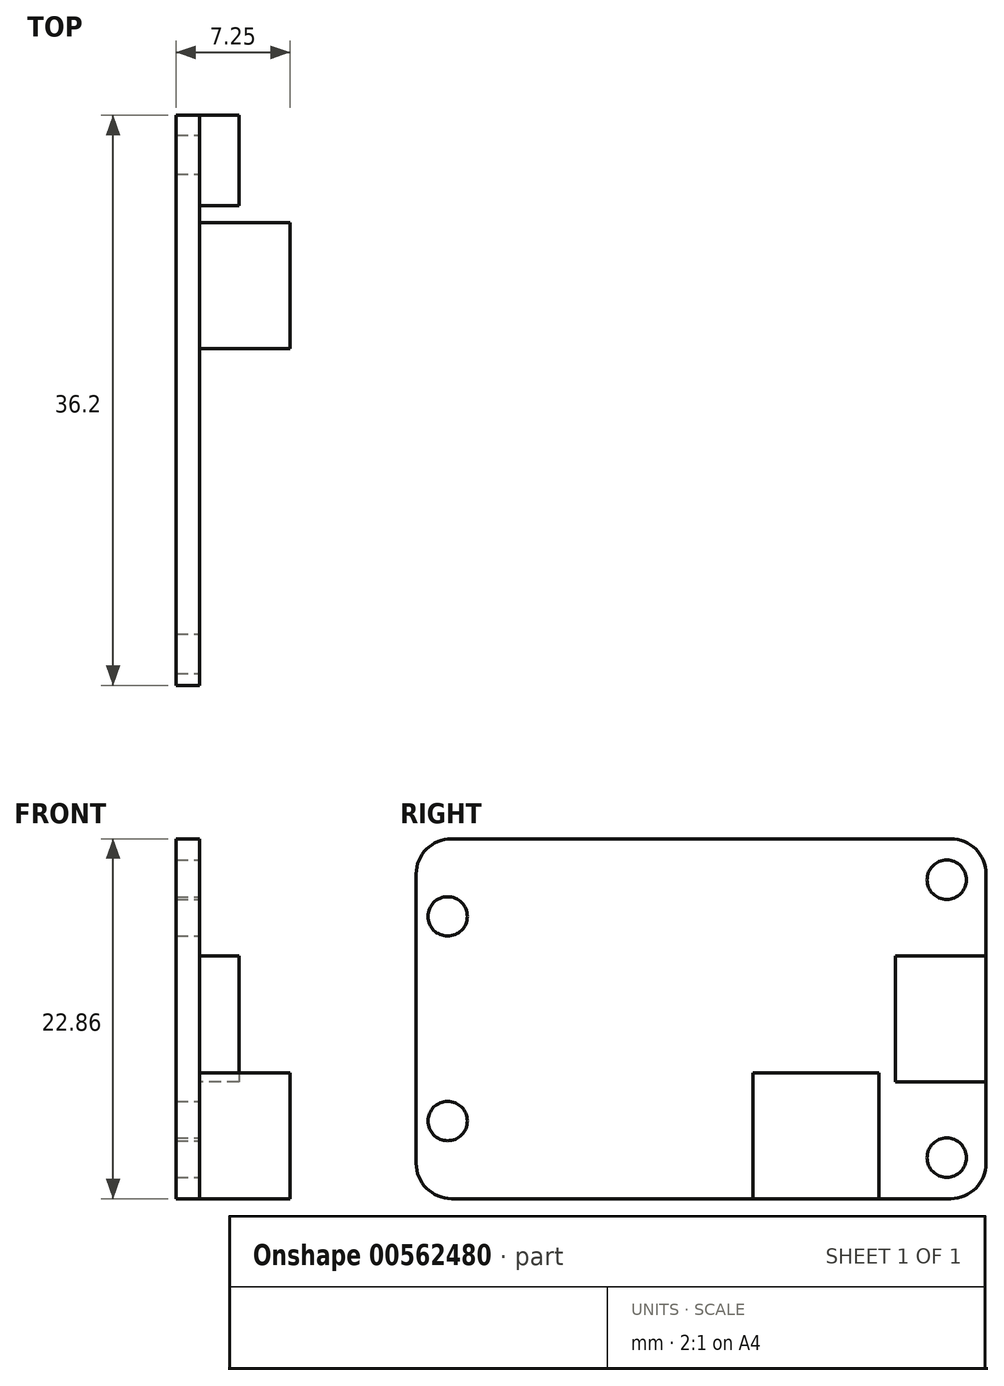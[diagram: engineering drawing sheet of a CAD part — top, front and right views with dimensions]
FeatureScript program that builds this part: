
annotation { "Feature Type Name" : "Feature", "Feature Type Description" : "" }
export const myFeature = defineFeature(function(context is Context, id is Id, definition is map)
    precondition{}
    {
        {
            var Q0;
            Q0=qCreatedBy(makeId("Right.planeOp"),FACE);
            var sketch = newSketch(context, id + "F0", { "sketchPlane" : qUnion([Q0])});
            skLineSegment(sketch, "E0.bottom", {"start": v(-18.1, 11.43) * mm, "end": v(18.1, 11.43) * mm});
            skLineSegment(sketch, "E0.top", {"start": v(-18.1, -11.43) * mm, "end": v(18.1, -11.43) * mm});
            skLineSegment(sketch, "E0.left", {"start": v(-18.1, 11.43) * mm, "end": v(-18.1, -11.43) * mm});
            skLineSegment(sketch, "E0.right", {"start": v(18.1, 11.43) * mm, "end": v(18.1, -11.43) * mm});
            skPoint(sketch, "E0.middle", {"position": v(0, 0) * mm});
            skSolve(sketch);
        }
        {
            var Q0;
            Q0=makeQuery(id+"F0.imprint","IMPRINT",FACE,{"disambiguationData":[TD([[makeQuery(id+"F0.imprint","IMPRINT",EDGE,{"derivedFrom":sQuery(id+"F0.wireOp",EDGE,"E0.bottom")}),-1.0]])]});
            extrude(context, id + "F1", {"entities" : qUnion([Q0]), "depth" : 1.5 * mm, "offsetDistance" : 25 * mm, "symmetric" : true});
        }
        {
            var Q0;
            Q0=makeQuery(id+"F1.opExtrude","CAP_FACE",FACE,{"disambiguationData":[OSD([sQuery(id+"F0.wireOp",EDGE,"E0.bottom"),sQuery(id+"F0.wireOp",EDGE,"E0.top"),sQuery(id+"F0.wireOp",EDGE,"E0.left"),sQuery(id+"F0.wireOp",EDGE,"E0.right")])],"isStart":false});
            var sketch = newSketch(context, id + "F2", { "sketchPlane" : qUnion([Q0])});
            skLineSegment(sketch, "E1.bottom", {"start": v(11.3, -11.43) * mm, "end": v(3.3, -11.43) * mm});
            skLineSegment(sketch, "E1.top", {"start": v(11.3, -3.43) * mm, "end": v(3.3, -3.43) * mm});
            skLineSegment(sketch, "E1.left", {"start": v(11.3, -11.43) * mm, "end": v(11.3, -3.43) * mm});
            skLineSegment(sketch, "E1.right", {"start": v(3.3, -11.43) * mm, "end": v(3.3, -3.43) * mm});
            skLineSegment(sketch, "E2.bottom", {"start": v(18.1, 4) * mm, "end": v(12.35, 4) * mm});
            skLineSegment(sketch, "E2.top", {"start": v(18.1, -4) * mm, "end": v(12.35, -4) * mm});
            skLineSegment(sketch, "E2.left", {"start": v(18.1, 4) * mm, "end": v(18.1, -4) * mm});
            skLineSegment(sketch, "E2.right", {"start": v(12.35, 4) * mm, "end": v(12.35, -4) * mm});
            skPoint(sketch, "E2.middle", {"position": v(15.23, 0) * mm});
            skSolve(sketch);
        }
        {
            var Q0;
            Q0=makeQuery(id+"F2.imprint","IMPRINT",FACE,{"disambiguationData":[TD([[makeQuery(id+"F2.imprint","IMPRINT",EDGE,{"derivedFrom":sQuery(id+"F2.wireOp",EDGE,"E1.bottom")}),1.0]])]});
            extrude(context, id + "F3", {"entities" : qUnion([Q0]), "operationType" : NewBodyOperationType.ADD, "depth" : 5.75 * mm, "offsetDistance" : 25 * mm});
        }
        {
            var Q0;
            Q0=makeQuery(id+"F2.imprint","IMPRINT",FACE,{"disambiguationData":[TD([[makeQuery(id+"F2.imprint","IMPRINT",EDGE,{"derivedFrom":sQuery(id+"F2.wireOp",EDGE,"E2.bottom")}),1.0]])]});
            extrude(context, id + "F4", {"entities" : qUnion([Q0]), "operationType" : NewBodyOperationType.ADD, "depth" : 2.5 * mm, "offsetDistance" : 25 * mm});
        }
        {
            var Q0;
            Q0=makeQuery(id+"F1.opExtrude","SWEPT_EDGE",EDGE,{"disambiguationData":[OSD([sQuery(id+"F0.wireOp",EDGE,"E0.bottom"),sQuery(id+"F0.wireOp",EDGE,"E0.left")])]});
            var Q1;
            Q1=makeQuery(id+"F1.opExtrude","SWEPT_EDGE",EDGE,{"disambiguationData":[OSD([sQuery(id+"F0.wireOp",EDGE,"E0.bottom"),sQuery(id+"F0.wireOp",EDGE,"E0.right")])]});
            var Q2;
            Q2=makeQuery(id+"F1.opExtrude","SWEPT_EDGE",EDGE,{"disambiguationData":[OSD([sQuery(id+"F0.wireOp",EDGE,"E0.top"),sQuery(id+"F0.wireOp",EDGE,"E0.right")])]});
            var Q3;
            Q3=makeQuery(id+"F1.opExtrude","SWEPT_EDGE",EDGE,{"disambiguationData":[OSD([sQuery(id+"F0.wireOp",EDGE,"E0.top"),sQuery(id+"F0.wireOp",EDGE,"E0.left")])]});
            fillet(context, id + "F5", {"entities" : qUnion([Q0, Q1, Q2, Q3]), "radius" : 2.25 * mm, "tangentPropagation" : true, "allowEdgeOverflow" : false});
        }
        {
            var Q0;
            Q0=makeQuery(id+"F2.imprint","IMPRINT",FACE,{"disambiguationData":[TD([[makeQuery(id+"F2.imprint","IMPRINT",EDGE,{"derivedFrom":sQuery(id+"F2.wireOp",EDGE,"E1.top")}),-1.0]])]});
            var sketch = newSketch(context, id + "F6", { "sketchPlane" : qUnion([Q0])});
            skCircle(sketch, "E3", {"center": v(15.6, 8.82) * mm, "radius": 1.25 * mm});
            skCircle(sketch, "E4", {"center": v(15.6, -8.83) * mm, "radius": 1.25 * mm});
            skCircle(sketch, "E5", {"center": v(-16.1, 6.5) * mm, "radius": 1.25 * mm});
            skCircle(sketch, "E6", {"center": v(-16.1, -6.5) * mm, "radius": 1.25 * mm});
            skSolve(sketch);
        }
        {
            var Q0;
            Q0 = qSketchRegion(id + "F6", true);
            var Q1;
            Q1=makeQuery(id+"F1.opExtrude","CAP_FACE",FACE,{"disambiguationData":[OSD([sQuery(id+"F0.wireOp",EDGE,"E0.bottom"),sQuery(id+"F0.wireOp",EDGE,"E0.top"),sQuery(id+"F0.wireOp",EDGE,"E0.left"),sQuery(id+"F0.wireOp",EDGE,"E0.right")])],"isStart":true});
            extrude(context, id + "F7", {"entities" : qUnion([Q0]), "operationType" : NewBodyOperationType.REMOVE, "endBound" : BoundingType.UP_TO_SURFACE, "oppositeDirection" : true, "depth" : 25 * mm, "endBoundEntityFace" : qUnion([Q1]), "offsetDistance" : 25 * mm});
        }
    });
